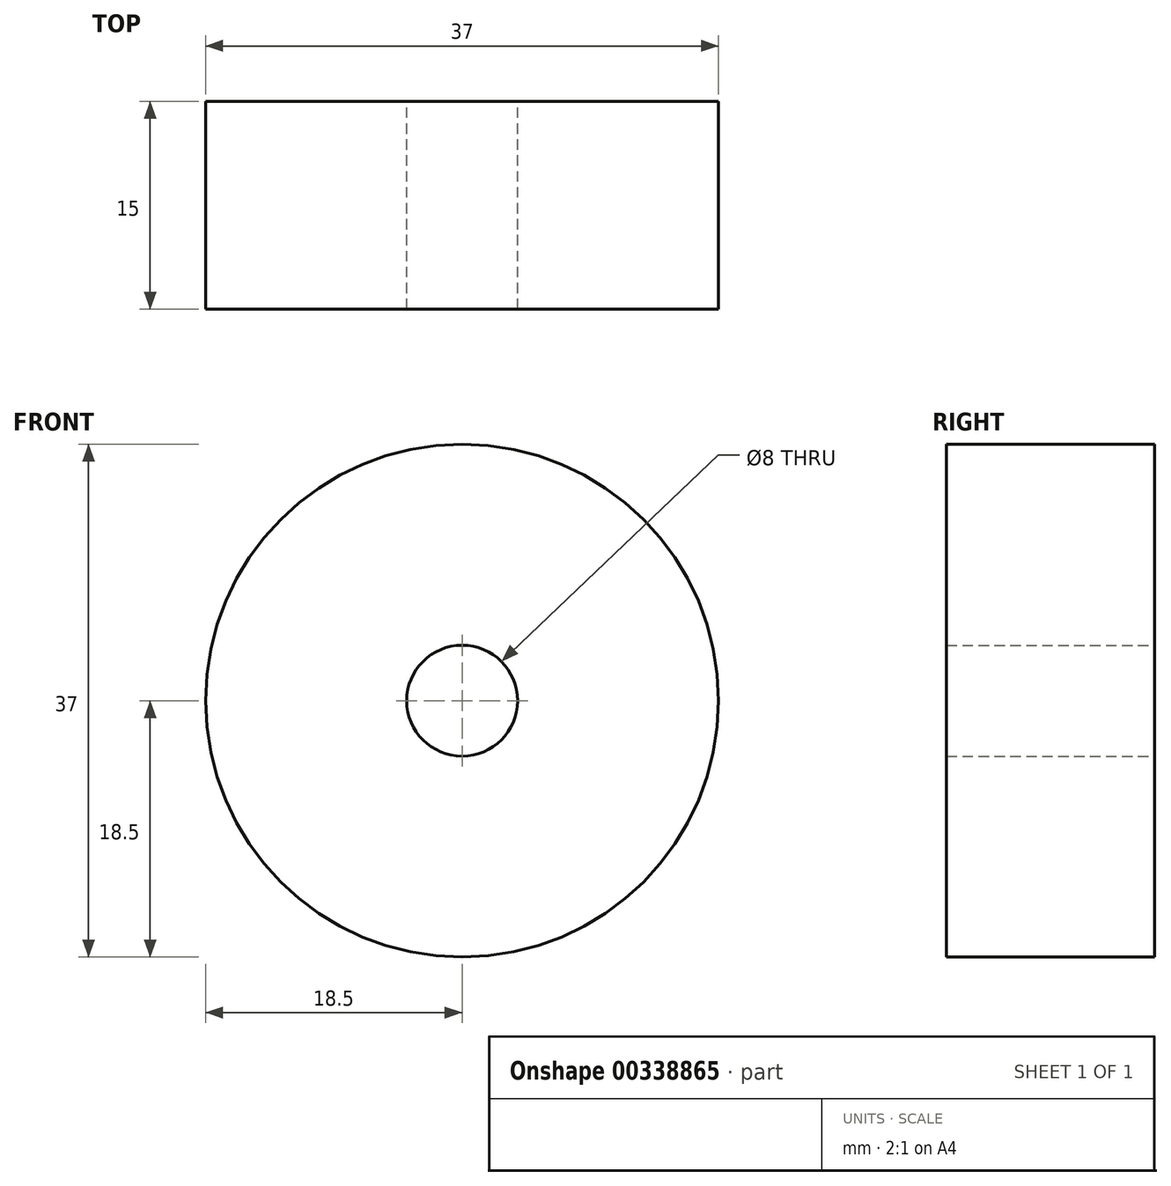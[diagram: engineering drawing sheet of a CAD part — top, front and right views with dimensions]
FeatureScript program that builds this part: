
annotation { "Feature Type Name" : "Feature", "Feature Type Description" : "" }
export const myFeature = defineFeature(function(context is Context, id is Id, definition is map)
    precondition{}
    {
        {
            var Q0;
            Q0=qCreatedBy(makeId("Front.planeOp"),FACE);
            var sketch = newSketch(context, id + "F0", { "sketchPlane" : qUnion([Q0])});
            skCircle(sketch, "E0", {"center": v(0, 0) * mm, "radius": 18.5 * mm});
            skCircle(sketch, "E1", {"center": v(0, 0) * mm, "radius": 4 * mm});
            skSolve(sketch);
        }
        {
            var Q0;
            Q0 = qSketchRegion(id + "F0", true);
            extrude(context, id + "F1", {"entities" : qUnion([Q0]), "depth" : 15 * mm});
        }
    });
